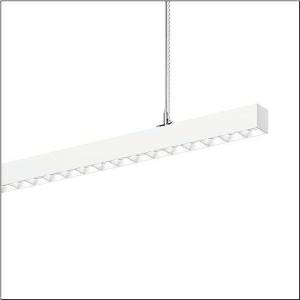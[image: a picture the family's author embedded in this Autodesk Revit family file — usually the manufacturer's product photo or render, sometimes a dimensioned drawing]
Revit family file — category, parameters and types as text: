
# Revit family: silica_r__21_51mx36dc3dwb_b05b
name_source: partatom
category: Lighting Fixtures
units: mm (PartAtom-declared; Revit-internal decimal feet)

## family parameters
Cut with Voids When Loaded = No
Host = Face
Light Source = No
Part Type = Normal
Room Calculation Point = No
Round Connector Dimension = Use Diameter
Shared = No

## types (1)
- --- (1 x LED, 17650 lm, 104.1 W, 3000K)
    Apparent Load = 104 VA
    CIE Flux Codes = 83 98 100 61 100
    Color Rendering = 80
    Color Temperature = 3000K
    Default Elevation = 1800 mm
    Description = Silica® 21, office luminaire, primary light control with darklight reflector, of PMMA, white, CAT 2 (L<= 3000cd/m²), light emission: direct/indirect distribution, primary light characteristic: symmetric, installation type: suspended mounting, LED, rated luminous flux: 17.650lm, luminous efficacy: 170lm/W, light colour: 830, colour temperature: 3000K, with terminal, 3+2-pole, max. 2.5mm², mains connection: 220..240V, AC, 50/60Hz, rated input power: 104.1W, luminaire housing, of aluminium, traffic white (RAL 9016), length: 3.004mm, width: 53mm, height: 53mm, protection rating (complete): IP20, insulation class (complete): insulation class I (protective earthing), certification: CE, permissible operating ambient temperature: 0..+35°C, standard: EN 50419, packaging unit: 1 piece
    Height = 53 mm
    Lamp = 1 x LED
    Lamp Light Flux = 17650 lm
    Lamp Power = 104.1 W
    Lamp count = 1
    Length = 3004 mm
    Luminous efficacy = 170 lm/W
    Manufacturer = Siteco
    ModVariant = No
    Model = 51MX36DC3DWB
    Mounting Place = Ceiling
    Mounting Type = Pendant
    Number of Poles = 1
    OnlyDefault = Yes
    Power Factor = 1
    Product Name = Silica® 21
    Product group = office luminaire | ceiling pendant
    ProductGroupID = 905
    Protection Class = Protection class I
    Protection Degree = IP 20
    RLX_Detail_Level = 1
    RlxData = <blob elided: 61741 chars, md5=08e2fd26>
    Socket = socket
    Standby Power = 0 W
    System Light Flux = 17650 lm
    System Power = 104 W
    Type Comments = factory setting: luminous flux: 100 % | dim-lin: 254 | 359 mA
    Type Image = l_1251641.jpg
    URL = http://relux.com
    VarID = @adj_030497
    Voltage = 0 V
    Weight = 0.00 kg
    Width = 53 mm

## geometry (parser evidence)
native form markers: Blend x4, Sweep x13
no freeform markers — native parametric forms only
